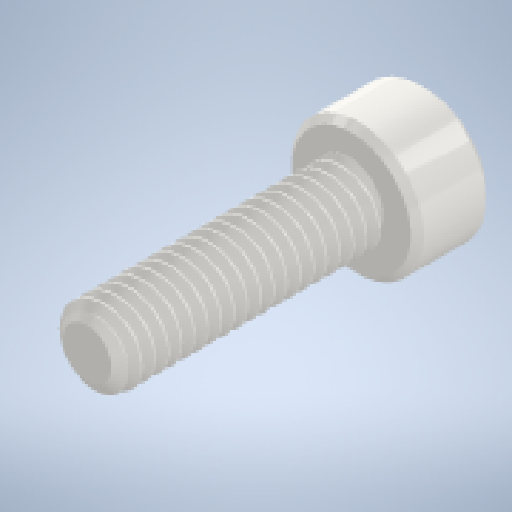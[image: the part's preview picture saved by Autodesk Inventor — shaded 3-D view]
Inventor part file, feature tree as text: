
AUTODESK INVENTOR PART (.ipt)
format: ipt  version: 2023 (Build 270158000, 158)  size: 699,904 bytes
history: native  units: in
note: dims shown in document units (in); Inventor stores cm internally (conversion verified against a paired STEP export)
features: chamfer x1
ambient origin geometry x8: Origin, YZ Plane, XZ Plane, XY Plane, X Axis, Y Axis, Z Axis, Center Point
bodies: Solid1 (feature_tree)
feature tree (1):
  chamfer  "Chamfer1"  [1 undecoded]
note: 1 required parameter value undecoded (feature->parameter linkage not recoverable at this tier; creation-order binding heuristic only, values carry confidence <= 0.55)
